# Revit family: XEW4-632-CA-N-3EHLU
name_source: partatom
category: Lighting Fixtures
revit_build: Autodesk Revit Architecture 2012 (Build: 20110309_2315(x64)
units: mm (PartAtom-declared; Revit-internal decimal feet)

## types (1)
- XEW4-632-CA-N-3EHLU
    Ballast = Lamp Eletronic, Instant Start
    Ballast Factor = 1.18 BF High Lumen 4' T8
    Color Filter = 16777215
    Default Elevation = 48"
    Description = XEW provides high light output in a wide, robust housing.
    Dimming Lamp Color Temperature Shift = Incandescent Lamp Curve
    Distribution = Narrow Distribution
    Emit Shape Visible in Rendering = No
    Emit from Rectangle Length = 48"
    Emit from Rectangle Width = 15"
    Finish = White
    IES Cat.No = XEW4-632-CA-N-3EHLU
    IES FILE LINK = http://www.columbialighting.com
    Lamp = LED
    Lamp Type = 4',T8-32,30,28
    Lens Type = Clear Impact Resistant Acrylic
    Manufacturer = Columbia Lighting
    Manufacturer Fax = (866)-898-1065
    Model = XEW4-632-CA-N-3EHLU
    No.of Lamps = 6
    Opal lens = Etched Glass
    Photometric Web File = 15376.ies
    Product Documentation Link = http://www.columbialighting.com
    Product Page URL = http://www.columbialighting.com
    Row Length = 48"
    Tilt Angle = 90.00°
    URL = http://www.columbialighting.com
    Voltage = 120V-277V
    Wattage Comments = 25W

## geometry (parser evidence)
native form markers: Sweep x2
no freeform markers — native parametric forms only
